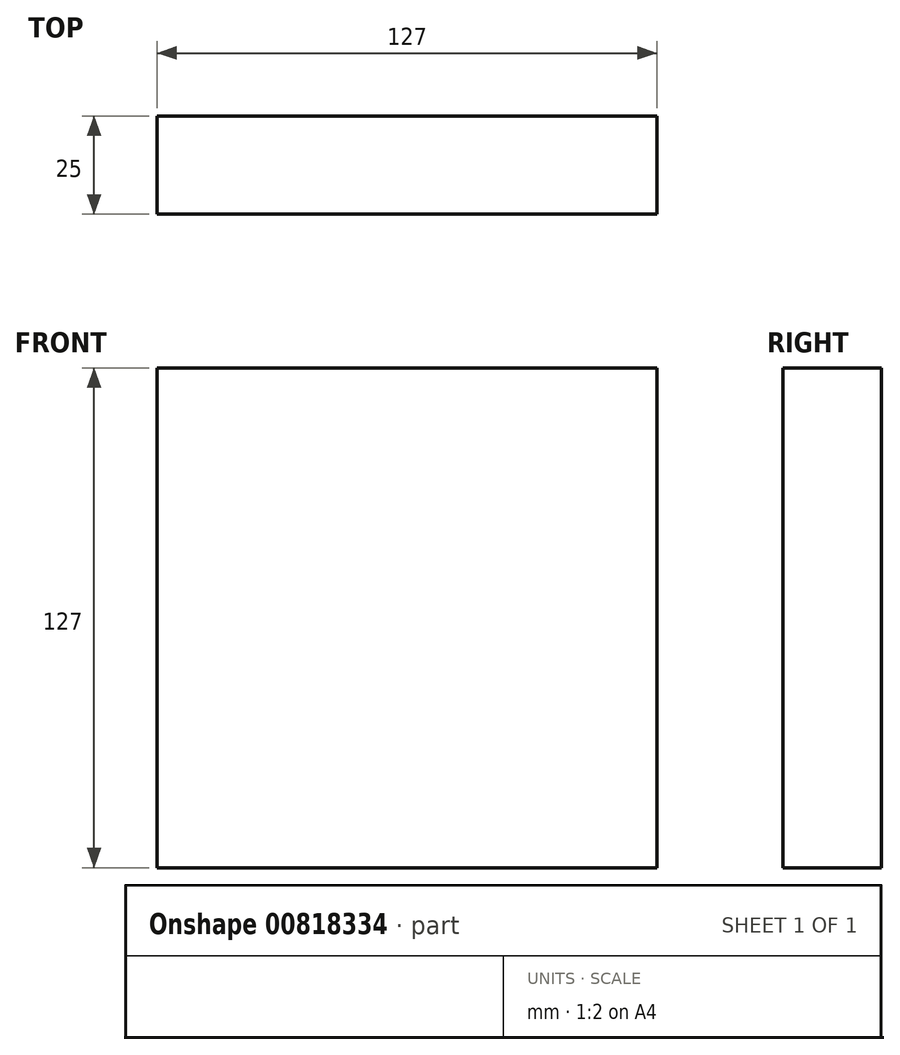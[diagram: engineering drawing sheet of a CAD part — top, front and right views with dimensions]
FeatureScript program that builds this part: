
annotation { "Feature Type Name" : "Feature", "Feature Type Description" : "" }
export const myFeature = defineFeature(function(context is Context, id is Id, definition is map)
    precondition{}
    {
        {
            var Q0;
            Q0=qCreatedBy(makeId("Front.planeOp"),FACE);
            var sketch = newSketch(context, id + "F0", { "sketchPlane" : qUnion([Q0])});
            skLineSegment(sketch, "E0.bottom", {"start": v(0, 0) * mm, "end": v(127, 0) * mm});
            skLineSegment(sketch, "E0.top", {"start": v(0, 127) * mm, "end": v(127, 127) * mm});
            skLineSegment(sketch, "E0.left", {"start": v(0, 0) * mm, "end": v(0, 127) * mm});
            skLineSegment(sketch, "E0.right", {"start": v(127, 0) * mm, "end": v(127, 127) * mm});
            skSolve(sketch);
        }
        {
            var Q0;
            Q0 = qSketchRegion(id + "F0", true);
            extrude(context, id + "F1", {"entities" : qUnion([Q0]), "depth" : 25 * mm, "offsetDistance" : 25 * mm});
        }
    });
